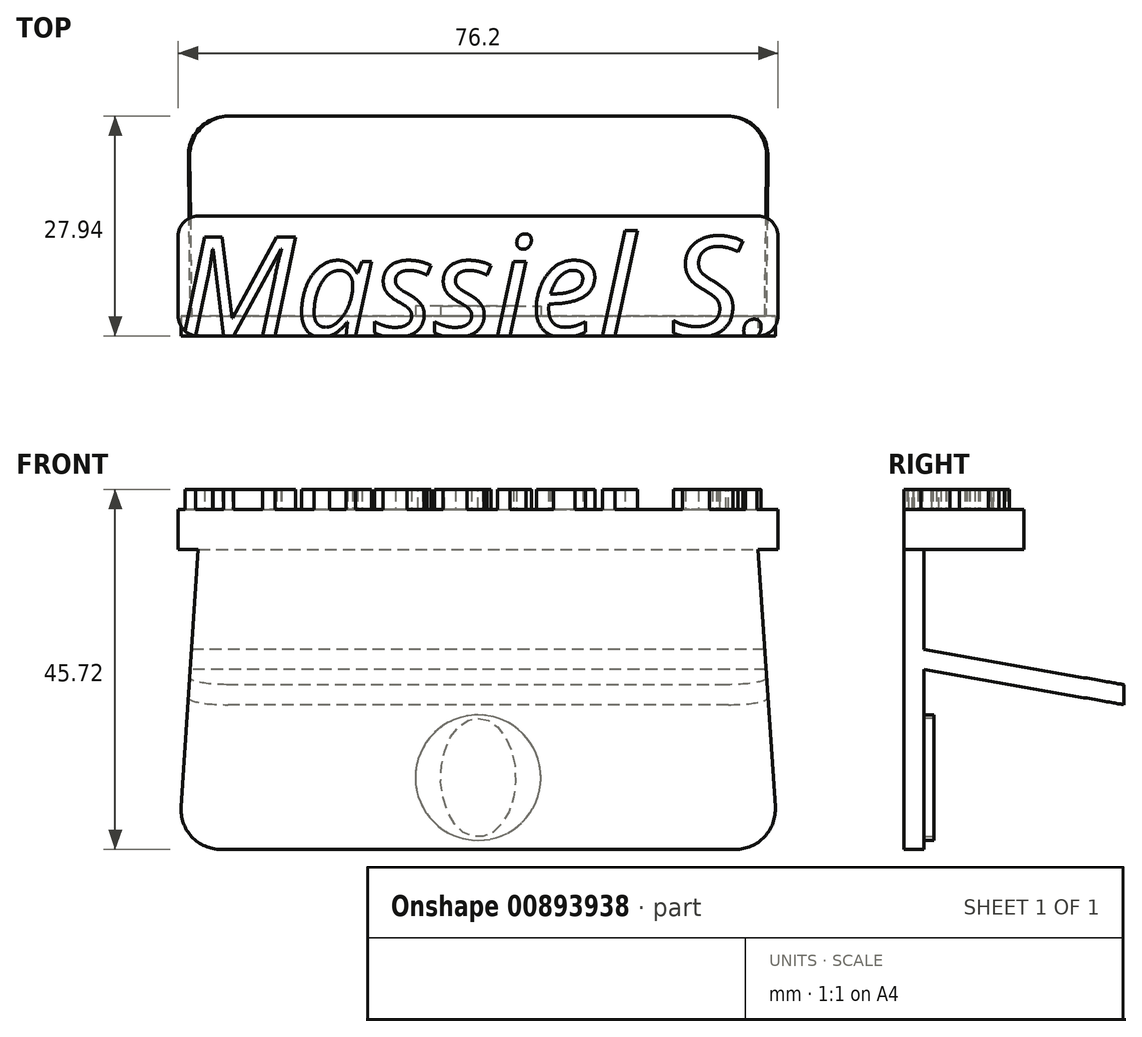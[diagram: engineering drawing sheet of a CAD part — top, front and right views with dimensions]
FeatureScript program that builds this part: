
annotation { "Feature Type Name" : "Feature", "Feature Type Description" : "" }
export const myFeature = defineFeature(function(context is Context, id is Id, definition is map)
    precondition{}
    {
        {
            var Q0;
            Q0=qCreatedBy(makeId("Top.planeOp"),FACE);
            var sketch = newSketch(context, id + "F0", { "sketchPlane" : qUnion([Q0])});
            skLineSegment(sketch, "E0.bottom", {"start": v(0, 0) * mm, "end": v(76.2, 0) * mm});
            skLineSegment(sketch, "E0.top", {"start": v(0, 15.24) * mm, "end": v(76.2, 15.24) * mm});
            skLineSegment(sketch, "E0.left", {"start": v(0, 0) * mm, "end": v(0, 15.24) * mm});
            skLineSegment(sketch, "E0.right", {"start": v(76.2, 0) * mm, "end": v(76.2, 15.24) * mm});
            skSolve(sketch);
        }
        {
            var Q0;
            Q0 = qSketchRegion(id + "F0", true);
            extrude(context, id + "F1", {"entities" : qUnion([Q0]), "depth" : 5.08 * mm, "offsetDistance" : 25.4 * mm});
        }
        {
            var Q0;
            Q0=makeQuery(id+"F1.opExtrude","CAP_FACE",FACE,{"disambiguationData":[OSD([sQuery(id+"F0.wireOp",EDGE,"E0.bottom"),sQuery(id+"F0.wireOp",EDGE,"E0.top"),sQuery(id+"F0.wireOp",EDGE,"E0.left"),sQuery(id+"F0.wireOp",EDGE,"E0.right")])],"isStart":false});
            var sketch = newSketch(context, id + "F2", { "sketchPlane" : qUnion([Q0])});
            skText(sketch, "E1", { "text": "Massiel S.", "fontName": "NotoSans-Italic.ttf"});
            const initialGuessF2  = {"E1": [0, 0, 1, 0, 0.0127]};
            skSetInitialGuess(sketch, initialGuessF2);
            skSolve(sketch);
        }
        {
            var Q0;
            Q0=makeQuery(id+"F2.imprint","IMPRINT",FACE,{"disambiguationData":[TD([[makeQuery(id+"F2.imprint","IMPRINT",EDGE,{"derivedFrom":sQuery(id+"F2.wireOp",EDGE,"E1.sketch_text.stroke-0")}),-1.0]])]});
            var Q1;
            {var subQ4=sQuery(id+"F2.wireOp",EDGE,"E1.sketch_text.stroke-19");Q1=makeQuery(id+"F2.imprint","IMPRINT",FACE,{"disambiguationData":[TD([[makeQuery(id+"F2.imprint","IMPRINT",EDGE,{"derivedFrom":subQ4}),-1.0]])]});}
            var Q2;
            {var subQ5=sQuery(id+"F2.wireOp",EDGE,"E1.sketch_text.stroke-43");Q2=makeQuery(id+"F2.imprint","IMPRINT",FACE,{"disambiguationData":[TD([[makeQuery(id+"F2.imprint","IMPRINT",EDGE,{"derivedFrom":subQ5}),-1.0]])]});}
            var Q3;
            {var subQ5=sQuery(id+"F2.wireOp",EDGE,"E1.sketch_text.stroke-68");Q3=makeQuery(id+"F2.imprint","IMPRINT",FACE,{"disambiguationData":[TD([[makeQuery(id+"F2.imprint","IMPRINT",EDGE,{"derivedFrom":subQ5}),-1.0]])]});}
            var Q4;
            Q4=makeQuery(id+"F2.imprint","IMPRINT",FACE,{"disambiguationData":[TD([[makeQuery(id+"F2.imprint","IMPRINT",EDGE,{"derivedFrom":sQuery(id+"F2.wireOp",EDGE,"E1.sketch_text.stroke-93")}),1.0]])]});
            var Q5;
            Q5=makeQuery(id+"F2.imprint","IMPRINT",FACE,{"disambiguationData":[TD([[makeQuery(id+"F2.imprint","IMPRINT",EDGE,{"derivedFrom":sQuery(id+"F2.wireOp",EDGE,"E1.sketch_text.stroke-97")}),-1.0]])]});
            var Q6;
            Q6=makeQuery(id+"F2.imprint","IMPRINT",FACE,{"disambiguationData":[TD([[makeQuery(id+"F2.imprint","IMPRINT",EDGE,{"derivedFrom":sQuery(id+"F2.wireOp",EDGE,"E1.sketch_text.stroke-104")}),-1.0]])]});
            var Q7;
            Q7=makeQuery(id+"F2.imprint","IMPRINT",FACE,{"disambiguationData":[TD([[makeQuery(id+"F2.imprint","IMPRINT",EDGE,{"derivedFrom":sQuery(id+"F2.wireOp",EDGE,"E1.sketch_text.stroke-129")}),1.0]])]});
            var Q8;
            {var subQ5=sQuery(id+"F2.wireOp",EDGE,"E1.sketch_text.stroke-133");Q8=makeQuery(id+"F2.imprint","IMPRINT",FACE,{"disambiguationData":[TD([[makeQuery(id+"F2.imprint","IMPRINT",EDGE,{"derivedFrom":subQ5}),-1.0]])]});}
            var Q9;
            {var subQ0=sQuery(id+"F2.wireOp",EDGE,"E1.sketch_text.stroke-158");Q9=makeQuery(id+"F2.imprint","IMPRINT",FACE,{"disambiguationData":[TD([[makeQuery(id+"F2.imprint","IMPRINT",EDGE,{"derivedFrom":subQ0}),-1.0]])]});}
            extrude(context, id + "F3", {"entities" : qUnion([Q0, Q1, Q2, Q3, Q4, Q5, Q6, Q7, Q8, Q9]), "operationType" : NewBodyOperationType.ADD, "depth" : 2.54 * mm, "offsetDistance" : 25.4 * mm});
        }
        {
            var Q0;
            Q0=makeQuery(id+"F1.opExtrude","SWEPT_EDGE",EDGE,{"disambiguationData":[OSD([sQuery(id+"F0.wireOp",EDGE,"E0.bottom"),sQuery(id+"F0.wireOp",EDGE,"E0.left")])]});
            var Q1;
            Q1=makeQuery(id+"F1.opExtrude","SWEPT_EDGE",EDGE,{"disambiguationData":[OSD([sQuery(id+"F0.wireOp",EDGE,"E0.top"),sQuery(id+"F0.wireOp",EDGE,"E0.left")])]});
            var Q2;
            Q2=makeQuery(id+"F1.opExtrude","SWEPT_EDGE",EDGE,{"disambiguationData":[OSD([sQuery(id+"F0.wireOp",EDGE,"E0.bottom"),sQuery(id+"F0.wireOp",EDGE,"E0.right")])]});
            var Q3;
            Q3=makeQuery(id+"F1.opExtrude","SWEPT_EDGE",EDGE,{"disambiguationData":[OSD([sQuery(id+"F0.wireOp",EDGE,"E0.top"),sQuery(id+"F0.wireOp",EDGE,"E0.right")])]});
            fillet(context, id + "F4", {"entities" : qUnion([Q0, Q1, Q2, Q3]), "radius" : 2.54 * mm, "tangentPropagation" : true, "allowEdgeOverflow" : false});
        }
        {
            var Q0;
            {var subQ0=sQuery(id+"F0.wireOp",EDGE,"E0.bottom");var subQ1=makeQuery(id+"F1.opExtrude","CAP_EDGE",EDGE,{"disambiguationData":[OSD([subQ0])],"isStart":false});Q0=makeQuery(id+"F3.boolean.opBoolean","MERGE",FACE,{"derivedFrom":[makeQuery(id+"F1.opExtrude","SWEPT_FACE",FACE,{"disambiguationData":[OSD([subQ0])]}),makeQuery(id+"F3.opExtrude","SWEPT_FACE",FACE,{"disambiguationData":[OSD([sQuery(id+"F2.wireOp",EDGE,"E1.sketch_text.stroke-3")])]}),makeQuery(id+"F3.opExtrude","SWEPT_FACE",FACE,{"disambiguationData":[OSD([sQuery(id+"F2.wireOp",EDGE,"E1.sketch_text.stroke-8")])]}),makeQuery(id+"F3.opExtrude","SWEPT_FACE",FACE,{"disambiguationData":[OSD([sQuery(id+"F2.wireOp",EDGE,"E1.sketch_text.stroke-13")])]}),makeQuery(id+"F3.opExtrude","SWEPT_FACE",FACE,{"disambiguationData":[OSD([sQuery(id+"F2.wireOp",EDGE,"E1.sketch_text.stroke-29")])]}),makeQuery(id+"F3.opExtrude","SWEPT_FACE",FACE,{"disambiguationData":[OSD([sQuery(id+"F2.wireOp",EDGE,"E1.sketch_text.stroke-93")])]}),makeQuery(id+"F3.opExtrude","SWEPT_FACE",FACE,{"disambiguationData":[OSD([sQuery(id+"F2.wireOp",EDGE,"E1.sketch_text.stroke-129")])]}),makeQuery(id+"F3.opExtrude","SWEPT_FACE",FACE,{"disambiguationData":[OSD([subQ0]),TDD([makeQuery(id+"F2.imprint","IMPRINT",EDGE,{"disambiguationData":[TD([[makeQuery(id+"F2.imprint","INTERSECT",VERTEX,{"derivedFrom":[subQ1,sQuery(id+"F2.wireOp",EDGE,"E1.sketch_text.stroke-18")]}),-1.0]])],"derivedFrom":subQ1})])]}),makeQuery(id+"F3.opExtrude","SWEPT_FACE",FACE,{"disambiguationData":[OSD([subQ0]),TDD([makeQuery(id+"F2.imprint","IMPRINT",EDGE,{"disambiguationData":[TD([[makeQuery(id+"F2.imprint","INTERSECT",VERTEX,{"derivedFrom":[subQ1,sQuery(id+"F2.wireOp",EDGE,"E1.sketch_text.stroke-44")]}),1.0]])],"derivedFrom":subQ1})])]}),makeQuery(id+"F3.opExtrude","SWEPT_FACE",FACE,{"disambiguationData":[OSD([subQ0]),TDD([makeQuery(id+"F2.imprint","IMPRINT",EDGE,{"disambiguationData":[TD([[makeQuery(id+"F2.imprint","INTERSECT",VERTEX,{"derivedFrom":[subQ1,sQuery(id+"F2.wireOp",EDGE,"E1.sketch_text.stroke-69")]}),1.0]])],"derivedFrom":subQ1})])]}),makeQuery(id+"F3.opExtrude","SWEPT_FACE",FACE,{"disambiguationData":[OSD([subQ0]),TDD([makeQuery(id+"F2.imprint","IMPRINT",EDGE,{"disambiguationData":[TD([[makeQuery(id+"F2.imprint","INTERSECT",VERTEX,{"derivedFrom":[subQ1,sQuery(id+"F2.wireOp",EDGE,"E1.sketch_text.stroke-111")]}),-1.0]])],"derivedFrom":subQ1})])]}),makeQuery(id+"F3.opExtrude","SWEPT_FACE",FACE,{"disambiguationData":[OSD([subQ0]),TDD([makeQuery(id+"F2.imprint","IMPRINT",EDGE,{"disambiguationData":[TD([[makeQuery(id+"F2.imprint","INTERSECT",VERTEX,{"derivedFrom":[subQ1,sQuery(id+"F2.wireOp",EDGE,"E1.sketch_text.stroke-134")]}),1.0]])],"derivedFrom":subQ1})])]}),makeQuery(id+"F3.opExtrude","SWEPT_FACE",FACE,{"disambiguationData":[OSD([subQ0]),TDD([makeQuery(id+"F2.imprint","IMPRINT",EDGE,{"disambiguationData":[TD([[makeQuery(id+"F2.imprint","INTERSECT",VERTEX,{"derivedFrom":[subQ1,sQuery(id+"F2.wireOp",EDGE,"E1.sketch_text.stroke-163")]}),1.0]])],"derivedFrom":subQ1})])]})]});}
            var sketch = newSketch(context, id + "F5", { "sketchPlane" : qUnion([Q0])});
            skLineSegment(sketch, "E2", {"start": v(2.54, 0) * mm, "end": v(0, -38.1) * mm});
            skLineSegment(sketch, "E3", {"start": v(0, -38.1) * mm, "end": v(76.2, -38.1) * mm});
            skLineSegment(sketch, "E4", {"start": v(76.2, -38.1) * mm, "end": v(73.66, 0) * mm});
            skSolve(sketch);
        }
        {
            var Q0;
            Q0=makeQuery(id+"F5.imprint","IMPRINT",FACE,{"disambiguationData":[TD([[makeQuery(id+"F5.imprint","IMPRINT",EDGE,{"derivedFrom":sQuery(id+"F5.wireOp",EDGE,"E2")}),1.0]])]});
            extrude(context, id + "F6", {"entities" : qUnion([Q0]), "operationType" : NewBodyOperationType.ADD, "oppositeDirection" : true, "depth" : 2.54 * mm, "offsetDistance" : 25.4 * mm});
        }
        {
            var Q0;
            Q0=makeQuery(id+"F6.opExtrude","CAP_FACE",FACE,{"disambiguationData":[OSD([sQuery(id+"F0.wireOp",EDGE,"E0.bottom"),sQuery(id+"F5.wireOp",EDGE,"E2"),sQuery(id+"F5.wireOp",EDGE,"E3"),sQuery(id+"F5.wireOp",EDGE,"E4")])],"isStart":false});
            var sketch = newSketch(context, id + "F7", { "sketchPlane" : qUnion([Q0])});
            skLineSegment(sketch, "E5.bottom", {"start": v(-75.18, -22.86) * mm, "end": v(0, -22.86) * mm});
            skLineSegment(sketch, "E5.top", {"start": v(-75.18, -12.7) * mm, "end": v(0, -12.7) * mm});
            skLineSegment(sketch, "E5.left", {"start": v(-75.18, -22.86) * mm, "end": v(-75.18, -12.7) * mm});
            skLineSegment(sketch, "E5.right", {"start": v(0, -22.86) * mm, "end": v(0, -12.7) * mm});
            skSolve(sketch);
        }
        {
            var Q0;
            {var subQ1=makeQuery(id+"F6.opExtrude","CAP_EDGE",EDGE,{"disambiguationData":[OSD([sQuery(id+"F5.wireOp",EDGE,"E4")])],"isStart":false});var subQ5=sQuery(id+"F7.wireOp",EDGE,"E5.top");var subQ6=makeQuery(id+"F7.imprint","INTERSECT",VERTEX,{"derivedFrom":[subQ1,subQ5]});Q0=makeQuery(id+"F7.imprint","IMPRINT",FACE,{"disambiguationData":[TD([[makeQuery(id+"F7.imprint","IMPRINT",EDGE,{"disambiguationData":[TD([[subQ6,-1.0]])],"derivedFrom":subQ5}),-1.0]])]});}
            var Q1;
            {var subQ0=sQuery(id+"F7.wireOp",EDGE,"E5.right");Q1=makeQuery(id+"F7.imprint","IMPRINT",FACE,{"disambiguationData":[TD([[makeQuery(id+"F7.imprint","IMPRINT",EDGE,{"derivedFrom":subQ0}),1.0]])]});}
            var Q2;
            {var subQ0=sQuery(id+"F7.wireOp",EDGE,"E5.left");Q2=makeQuery(id+"F7.imprint","IMPRINT",FACE,{"disambiguationData":[TD([[makeQuery(id+"F7.imprint","IMPRINT",EDGE,{"derivedFrom":subQ0}),-1.0]])]});}
            extrude(context, id + "F8", {"entities" : qUnion([Q0, Q1, Q2]), "operationType" : NewBodyOperationType.ADD, "depth" : 25.4 * mm, "offsetDistance" : 25.4 * mm});
        }
        {
            var Q0;
            Q0=makeQuery(id+"F8.opExtrude","SWEPT_FACE",FACE,{"disambiguationData":[OSD([sQuery(id+"F7.wireOp",EDGE,"E5.right")])]});
            var sketch = newSketch(context, id + "F9", { "sketchPlane" : qUnion([Q0])});
            skLineSegment(sketch, "E6", {"start": v(-27.94, -17.18) * mm, "end": v(-27.94, -19.72) * mm});
            skLineSegment(sketch, "E7", {"start": v(-27.94, -19.72) * mm, "end": v(-2.54, -15.24) * mm});
            skLineSegment(sketch, "E8", {"start": v(-2.54, -15.24) * mm, "end": v(-2.54, -12.7) * mm});
            skLineSegment(sketch, "E9", {"start": v(-2.54, -12.7) * mm, "end": v(-27.94, -17.18) * mm});
            skSolve(sketch);
        }
        {
            var Q0;
            {var subQ0=sQuery(id+"F9.wireOp",EDGE,"E9");Q0=makeQuery(id+"F9.imprint","IMPRINT",FACE,{"disambiguationData":[TD([[makeQuery(id+"F9.imprint","IMPRINT",EDGE,{"derivedFrom":subQ0}),-1.0]])]});}
            var Q1;
            {var subQ0=sQuery(id+"F9.wireOp",EDGE,"E7");Q1=makeQuery(id+"F9.imprint","IMPRINT",FACE,{"disambiguationData":[TD([[makeQuery(id+"F9.imprint","IMPRINT",EDGE,{"derivedFrom":subQ0}),-1.0]])]});}
            extrude(context, id + "F10", {"entities" : qUnion([Q0, Q1]), "operationType" : NewBodyOperationType.REMOVE, "endBound" : BoundingType.THROUGH_ALL, "oppositeDirection" : true, "depth" : 25.4 * mm, "offsetDistance" : 25.4 * mm});
        }
        {
            var Q0;
            {var subQ0=sQuery(id+"F0.wireOp",EDGE,"E0.bottom");var subQ1=makeQuery(id+"F1.opExtrude","CAP_EDGE",EDGE,{"disambiguationData":[OSD([subQ0])],"isStart":false});Q0=makeQuery(id+"F6.boolean.opBoolean","MERGE",FACE,{"derivedFrom":[makeQuery(id+"F3.boolean.opBoolean","MERGE",FACE,{"derivedFrom":[makeQuery(id+"F1.opExtrude","SWEPT_FACE",FACE,{"disambiguationData":[OSD([subQ0])]}),makeQuery(id+"F3.opExtrude","SWEPT_FACE",FACE,{"disambiguationData":[OSD([sQuery(id+"F2.wireOp",EDGE,"E1.sketch_text.stroke-3")])]}),makeQuery(id+"F3.opExtrude","SWEPT_FACE",FACE,{"disambiguationData":[OSD([sQuery(id+"F2.wireOp",EDGE,"E1.sketch_text.stroke-8")])]}),makeQuery(id+"F3.opExtrude","SWEPT_FACE",FACE,{"disambiguationData":[OSD([sQuery(id+"F2.wireOp",EDGE,"E1.sketch_text.stroke-13")])]}),makeQuery(id+"F3.opExtrude","SWEPT_FACE",FACE,{"disambiguationData":[OSD([sQuery(id+"F2.wireOp",EDGE,"E1.sketch_text.stroke-29")])]}),makeQuery(id+"F3.opExtrude","SWEPT_FACE",FACE,{"disambiguationData":[OSD([sQuery(id+"F2.wireOp",EDGE,"E1.sketch_text.stroke-93")])]}),makeQuery(id+"F3.opExtrude","SWEPT_FACE",FACE,{"disambiguationData":[OSD([sQuery(id+"F2.wireOp",EDGE,"E1.sketch_text.stroke-129")])]}),makeQuery(id+"F3.opExtrude","SWEPT_FACE",FACE,{"disambiguationData":[OSD([subQ0]),TDD([makeQuery(id+"F2.imprint","IMPRINT",EDGE,{"disambiguationData":[TD([[makeQuery(id+"F2.imprint","INTERSECT",VERTEX,{"derivedFrom":[subQ1,sQuery(id+"F2.wireOp",EDGE,"E1.sketch_text.stroke-18")]}),-1.0]])],"derivedFrom":subQ1})])]}),makeQuery(id+"F3.opExtrude","SWEPT_FACE",FACE,{"disambiguationData":[OSD([subQ0]),TDD([makeQuery(id+"F2.imprint","IMPRINT",EDGE,{"disambiguationData":[TD([[makeQuery(id+"F2.imprint","INTERSECT",VERTEX,{"derivedFrom":[subQ1,sQuery(id+"F2.wireOp",EDGE,"E1.sketch_text.stroke-44")]}),1.0]])],"derivedFrom":subQ1})])]}),makeQuery(id+"F3.opExtrude","SWEPT_FACE",FACE,{"disambiguationData":[OSD([subQ0]),TDD([makeQuery(id+"F2.imprint","IMPRINT",EDGE,{"disambiguationData":[TD([[makeQuery(id+"F2.imprint","INTERSECT",VERTEX,{"derivedFrom":[subQ1,sQuery(id+"F2.wireOp",EDGE,"E1.sketch_text.stroke-69")]}),1.0]])],"derivedFrom":subQ1})])]}),makeQuery(id+"F3.opExtrude","SWEPT_FACE",FACE,{"disambiguationData":[OSD([subQ0]),TDD([makeQuery(id+"F2.imprint","IMPRINT",EDGE,{"disambiguationData":[TD([[makeQuery(id+"F2.imprint","INTERSECT",VERTEX,{"derivedFrom":[subQ1,sQuery(id+"F2.wireOp",EDGE,"E1.sketch_text.stroke-111")]}),-1.0]])],"derivedFrom":subQ1})])]}),makeQuery(id+"F3.opExtrude","SWEPT_FACE",FACE,{"disambiguationData":[OSD([subQ0]),TDD([makeQuery(id+"F2.imprint","IMPRINT",EDGE,{"disambiguationData":[TD([[makeQuery(id+"F2.imprint","INTERSECT",VERTEX,{"derivedFrom":[subQ1,sQuery(id+"F2.wireOp",EDGE,"E1.sketch_text.stroke-134")]}),1.0]])],"derivedFrom":subQ1})])]}),makeQuery(id+"F3.opExtrude","SWEPT_FACE",FACE,{"disambiguationData":[OSD([subQ0]),TDD([makeQuery(id+"F2.imprint","IMPRINT",EDGE,{"disambiguationData":[TD([[makeQuery(id+"F2.imprint","INTERSECT",VERTEX,{"derivedFrom":[subQ1,sQuery(id+"F2.wireOp",EDGE,"E1.sketch_text.stroke-163")]}),1.0]])],"derivedFrom":subQ1})])]})]}),makeQuery(id+"F6.opExtrude","CAP_FACE",FACE,{"disambiguationData":[OSD([subQ0,sQuery(id+"F5.wireOp",EDGE,"E2"),sQuery(id+"F5.wireOp",EDGE,"E3"),sQuery(id+"F5.wireOp",EDGE,"E4")])],"isStart":true})]});}
            var sketch = newSketch(context, id + "F11", { "sketchPlane" : qUnion([Q0])});
            skLineSegment(sketch, "E10", {"start": v(1.2, -20.08) * mm, "end": v(-1.16, -20.08) * mm});
            skLineSegment(sketch, "E11", {"start": v(-1.16, -20.08) * mm, "end": v(-1.16, -12.56) * mm});
            skLineSegment(sketch, "E12", {"start": v(-1.16, -12.56) * mm, "end": v(1.7, -12.56) * mm});
            skLineSegment(sketch, "E13", {"start": v(1.7, -12.56) * mm, "end": v(1.2, -20.08) * mm});
            skLineSegment(sketch, "E14", {"start": v(75.08, -21.3) * mm, "end": v(74.37, -10.7) * mm});
            skLineSegment(sketch, "E15", {"start": v(74.37, -10.7) * mm, "end": v(76.43, -10.7) * mm});
            skLineSegment(sketch, "E16", {"start": v(76.43, -10.7) * mm, "end": v(76.43, -21.27) * mm});
            skLineSegment(sketch, "E17", {"start": v(76.43, -21.27) * mm, "end": v(75.08, -21.3) * mm});
            skSolve(sketch);
        }
        {
            var Q0;
            Q0 = qSketchRegion(id + "F11", true);
            extrude(context, id + "F12", {"entities" : qUnion([Q0]), "operationType" : NewBodyOperationType.REMOVE, "endBound" : BoundingType.THROUGH_ALL, "oppositeDirection" : true, "depth" : 25.4 * mm, "offsetDistance" : 25.4 * mm});
        }
        {
            var Q0;
            Q0=makeQuery(id+"F6.opExtrude","SWEPT_EDGE",EDGE,{"disambiguationData":[OSD([sQuery(id+"F5.wireOp",EDGE,"E2"),sQuery(id+"F5.wireOp",EDGE,"E3")])]});
            var Q1;
            Q1=makeQuery(id+"F6.opExtrude","SWEPT_EDGE",EDGE,{"disambiguationData":[OSD([sQuery(id+"F5.wireOp",EDGE,"E3"),sQuery(id+"F5.wireOp",EDGE,"E4")])]});
            var Q2;
            Q2=makeQuery(id+"F12.boolean.opBoolean","INTERSECT",EDGE,{"derivedFrom":[makeQuery(id+"F8.opExtrude","CAP_FACE",FACE,{"disambiguationData":[OSD([sQuery(id+"F7.wireOp",EDGE,"E5.bottom"),sQuery(id+"F7.wireOp",EDGE,"E5.top"),sQuery(id+"F7.wireOp",EDGE,"E5.left"),sQuery(id+"F7.wireOp",EDGE,"E5.right")])],"isStart":false}),makeQuery(id+"F12.opExtrude","SWEPT_FACE",FACE,{"disambiguationData":[OSD([sQuery(id+"F11.wireOp",EDGE,"E14")])]})]});
            var Q3;
            Q3=makeQuery(id+"F12.boolean.opBoolean","INTERSECT",EDGE,{"derivedFrom":[makeQuery(id+"F8.opExtrude","CAP_FACE",FACE,{"disambiguationData":[OSD([sQuery(id+"F7.wireOp",EDGE,"E5.bottom"),sQuery(id+"F7.wireOp",EDGE,"E5.top"),sQuery(id+"F7.wireOp",EDGE,"E5.left"),sQuery(id+"F7.wireOp",EDGE,"E5.right")])],"isStart":false}),makeQuery(id+"F12.opExtrude","SWEPT_FACE",FACE,{"disambiguationData":[OSD([sQuery(id+"F11.wireOp",EDGE,"E13")])]})]});
            fillet(context, id + "F13", {"entities" : qUnion([Q0, Q1, Q2, Q3]), "radius" : 5.08 * mm, "tangentPropagation" : true, "allowEdgeOverflow" : false});
        }
        {
            var Q0;
            {var subQ0=sQuery(id+"F7.wireOp",EDGE,"E5.right");var subQ1=makeQuery(id+"F8.opExtrude","CAP_EDGE",EDGE,{"disambiguationData":[OSD([subQ0])],"isStart":true});var subQ2=sQuery(id+"F7.wireOp",EDGE,"E5.bottom");var subQ3=sQuery(id+"F5.wireOp",EDGE,"E4");var subQ4=sQuery(id+"F5.wireOp",EDGE,"E3");var subQ5=sQuery(id+"F5.wireOp",EDGE,"E2");Q0=makeQuery(id+"F10.boolean.opBoolean","MERGE",FACE,{"derivedFrom":[makeQuery(id+"F8.boolean.opBoolean","SPLIT",FACE,{"disambiguationData":[TD([makeQuery(id+"F6.opExtrude","SWEPT_FACE",FACE,{"disambiguationData":[OSD([subQ4])]})])],"derivedFrom":makeQuery(id+"F6.opExtrude","CAP_FACE",FACE,{"disambiguationData":[OSD([sQuery(id+"F0.wireOp",EDGE,"E0.bottom"),subQ5,subQ4,subQ3])],"isStart":false})})],"fromTools":[makeQuery(id+"F10.opExtrude","SWEPT_FACE",FACE,{"disambiguationData":[OSD([subQ0]),TDD([makeQuery(id+"F9.imprint","IMPRINT",EDGE,{"disambiguationData":[TD([[makeQuery(id+"F9.imprint","INTERSECT",VERTEX,{"derivedFrom":[makeQuery(id+"F8.opExtrude","SWEPT_EDGE",EDGE,{"disambiguationData":[OSD([subQ2,subQ0])]}),subQ1]}),-1.0]])],"derivedFrom":subQ1})])]})]});}
            var sketch = newSketch(context, id + "F14", { "sketchPlane" : qUnion([Q0])});
            skCircle(sketch, "E18", {"center": v(-38.1, -28.98) * mm, "radius": 7.97 * mm});
            skPoint(sketch, "E18.centerSnap0", {"position": v(-38.1, -38.1) * mm});
            skEllipse(sketch, "E19", {"center": v(-38.1, -28.98) * mm, "majorRadius": 7.55 * mm, "minorRadius": 4.77 * mm, "majorAxis": v(0, 1)});
            skSolve(sketch);
        }
        {
            var Q0;
            Q0=makeQuery(id+"F14.imprint","IMPRINT",FACE,{"disambiguationData":[TD([[makeQuery(id+"F14.imprint","IMPRINT",EDGE,{"derivedFrom":sQuery(id+"F14.wireOp",EDGE,"E18")}),1.0]])]});
            extrude(context, id + "F15", {"entities" : qUnion([Q0]), "operationType" : NewBodyOperationType.ADD, "depth" : 1.27 * mm, "offsetDistance" : 25.4 * mm});
        }
    });
